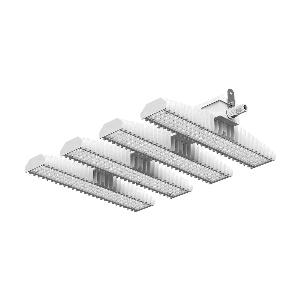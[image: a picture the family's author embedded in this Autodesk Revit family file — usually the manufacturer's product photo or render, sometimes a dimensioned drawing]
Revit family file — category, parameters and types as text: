
# Revit family: 3f_filippi_-_3f_lem_ho_medio_3f_filippi_-_58985_-_3f_lem_4_ho_led_280_dali_cr_medio
name_source: partatom
category: Lighting Fixtures
units: mm (PartAtom-declared; Revit-internal decimal feet)

## family parameters
Cut with Voids When Loaded = No
Host = Face
Light Source = No
Part Type = Normal
Room Calculation Point = No
Round Connector Dimension = Use Diameter
Shared = No

## types (1)
- 3F Filippi - 3F LEM HO Medio (1 x LED, 44256 lm, 276 W, 4000 K)
    Apparent Load = 276 VA
    Approval mark = CE
    CIE Flux Codes = 83 96 99 100 100
    Color Rendering = 80
    Color Temperature = 4000 K
    Control Gear = Electronic transformer
    Default Elevation = 1800 mm
    Description = Industrial luminaire with high light output and high luminous efficiency designed with the most innovative technologies for environments with temperature up to 55°C.

ILLUMINOTECHNICAL
Luminous efficiency 100% (DLOR 100%, ULOR 0%).
Initial luminous flux of the luminaire 44256 lm.
Medium distribution with rectangular shape.
Installation Interdistance Transv.D = 1.02 x hu - Long.D = 1.06 x hu.
Tabular UGR (CIE 117 - 4H-8H; S=0.25H; 70/50/20): RUG 20.2 - 19.8.
Beam angle: 65° - 67°.
Luminous efficacy 160 lm/W.
Lifetime (L93/B10): 30000 h. (tq+25°C)
Lifetime (L90/B10): 50000 h. (tq+25°C)
Lifetime (L85/B10): 80000 h. (tq+25°C)
Lifetime (L80/B10): 100000 h. (tq+25°C)
Lifetime (L85/B10): 50000 h. (tq+55°C)
Sudden decreased luminous flux after 50000 hours: 0% (C0).
Photobiological safety in compliance with IEC/TR 62778: RG0 risk exempt, (IEC 62471).
In compliance with IEC/EN 62722-2-1 - IEC/EN 62717 standards.

SOURCE
4 Mid-Power linear LED modules 70W/840.
Energy efficiency class (UE 2019/2020 - UE 2019/2015): C.
CIE 13.3 Colour rendering index: CRI >80 (R9 <50%).
IES TM-30 Fidelity Index: Rf = 84 Rg = 95.
CCT nominal colour temperature 4000 K.
Colour initial tolerance (MacAdam): SDCM 3.

MECHANICAL
Passive modular heatsinks in die-casted aluminium, painted in white colour.
To optimize the thermal management of the LED module, the heatsinks are oversized and provided with self-cleaning of cooling fins.
Wiring body in aluminium and galvanised steel anchored solidly to the sinks and thermally separated.
3F Lens lenses with high luminous efficiency, transparent methacrylate (PMMA), fixed to the LED modules.
Fixing brackets in stainless steel.
Luminaire with limited surface temperature. - D - (EN 60598-2-24)
Dimensions: 757x542 mm, height 129 mm. Weight 17.8 kg.
IP65 protection degree.
Mechanical strength to impacts IK06 (1 joule).
Glow-wire test resistance 650°C.

ELECTRICAL
Halogen Free DALI-2 DATI (Parts 251, 252, 253), PUSH-DIM, electronic wiring 230V-50/60Hz, power factor 0.97 at full load, THD <25%, constant output current, class I, 2 driver, 2 DALI addresses.
Power of the luminaire 276 W.
ENEC - CE.
SAFE FLICKER: PstLM=<1 and SVM=<0.4 (IEC TR 61547-1 and IEC TR 63158), to ensure a more comfortable and safe light.
Luminaire compliant with EN 60598-2-22 for power supply from a centralised emergency system CPSS (Central Power Supply System), not incorporated in the luminaire - high risk areas excluded. The default power and flux are 100% in AC and 15% in DC.
Ambient temperature from -30°C to +55°C.
Temperature class T6 max 85°C.
Quick connection via M25 5P connector with 9-13 mm tightening range.
Power unit positioned on a separate compartment by the LED module to ensure optimum temperatures of cabling components, to be inspectable and maintainable.
Relative humidity UR: <85%.

INSTALLATION
Ceiling / Suspended / Wall.
All accessories dedicated to this product are available on the Catalog and on our website www.3F-Filippi.com.

APPLICATIONS
In commercial environments, exhibition and industrial areas, stores, open areas.
Environments in which it is necessary a total protection against falling fragments (eg environments with foodstuffs or machines with moving parts or with extreme temperature changes), use luminaires with polycarbonate lenses.

LIGHT MANAGEMENT
Recommended minimum setting: 10%.
The luminaire, equipped with (DALI-2 DATI) driver, can be controlled manually with 3F Easy Dim technology or automatically/manually with wired or wireless DALI/D2D control systems.
The D2D driver guarantees interoperability with other devices with the same certification by making the following information available:
Device Data (Part 251), Energy Report (Part 252), Diagnosis & Maintenance (Part 253).
In electrical systems without a regulation system (manual or automatic) and DALI bus, a suitable jumper must be made on the DA-DA terminals of the appliance.

WARNING
Fixture not suitable for cold stores with an ambient temperature <0°C and/or relative humidity >85%.
Luminaire designed for disposal/recycling at end-of-life.
Replaceable (LED only) light source by a professional. Replaceable control gear by a professional.
    Height = 129 mm
    Lamp = 1 x LED
    Lamp Light Flux = 44256 lm
    Lamp Power = 276 W
    Lamp count = 1
    Length = 757 mm
    Lifetime = 50000 h
    Luminous efficacy = 160 lm/W
    Manufacturer = 3F Filippi
    ModVariant = No
    Model = 3F Filippi - 58985 - 3F LEM 4 HO LED 280 DALI CR MEDIO
    Mounting Place = Ceiling
    Mounting Type = Pendant
    Number of Poles = 1
    OnlyDefault = Yes
    Power Factor = 1
    Product Name = 3F Filippi - 3F LEM HO Medio
    Product group = pendant luminaire
    ProductGroupID = 9
    Protection Class = Protection class I
    Protection Degree = IP 65
    RLX_Detail_Level = 1
    RLX_Emergency_Light_Flux = 0 lm
    RLX_Emergency_Type = 0
    RLX_Emergency_Type_DB = No
    RlxData = <blob elided: 118257 chars, md5=d931d7ff>
    Socket = socket
    Standby Power = 0 W
    System Light Flux = 44256 lm
    System Power = 276 W
    Type Comments = Product without accessories
    Type Image = 3f_filippi_-_lem_4.jpg
    URL = http://relux.com
    VarID = ---
    Voltage = 0 V
    Weight = 0.00 kg
    Width = 542 mm

## geometry (parser evidence)
native form markers: Blend x4, Sweep x13
no freeform markers — native parametric forms only
